# Revit family: ECHO
name_source: partatom
category: Lighting Fixtures
revit_build: Autodesk Revit 2014 (Build: 20140709_2115(x64)
units: mm (PartAtom-declared; Revit-internal decimal feet)

## types (8) — shared parameters
Color Filter = 16777215
Dimming Lamp Color Temperature Shift = <None>
Emit Shape Visible in Rendering = No
Emit from Circle Diameter = 2' - 0"
Light Source Symbol Size = 2' - 0"

## per-type parameters (varying)
| type | A- 47x14-12 | A-35x14-12 | A-35x14-8 | A-47x14-8 | B-35x14-12 | B-35x14-8 | B-47x14-12 | B-47x14-8 | Diffuser |
| Fin Type A - 35"D x 14"H-8 Fins | No | No | Yes | No | No | No | No | No | <By Category> |
| Fin Type A - 47"D x 14"H-8 Fins | No | No | No | Yes | No | No | No | No | <By Category> |
| Fin Type A - 47"D x 14"H-12 Fins | Yes | No | No | No | No | No | No | No | <By Category> |
| Fin Type A - 35"D x 14"H-12 Fins | No | Yes | No | No | No | No | No | No | <By Category> |
| Fin Type B - 35"D x 14"H-12 Fins | No | No | No | No | Yes | No | No | No | <By Category> |
| Fin Type B - 35"D x 14"H-8 Fins | No | No | No | No | No | Yes | No | No | <By Category> |
| Fin Type B - 47"D x 14"H-12 Fins | No | No | No | No | No | No | Yes | No | <By Category> |
| Fin Type B - 47"D x 14"H-8 Fins | No | No | No | No | No | No | No | Yes | White Opal Acrylic |

## geometry (parser evidence)
native form markers: Sweep x51
no freeform markers — native parametric forms only
